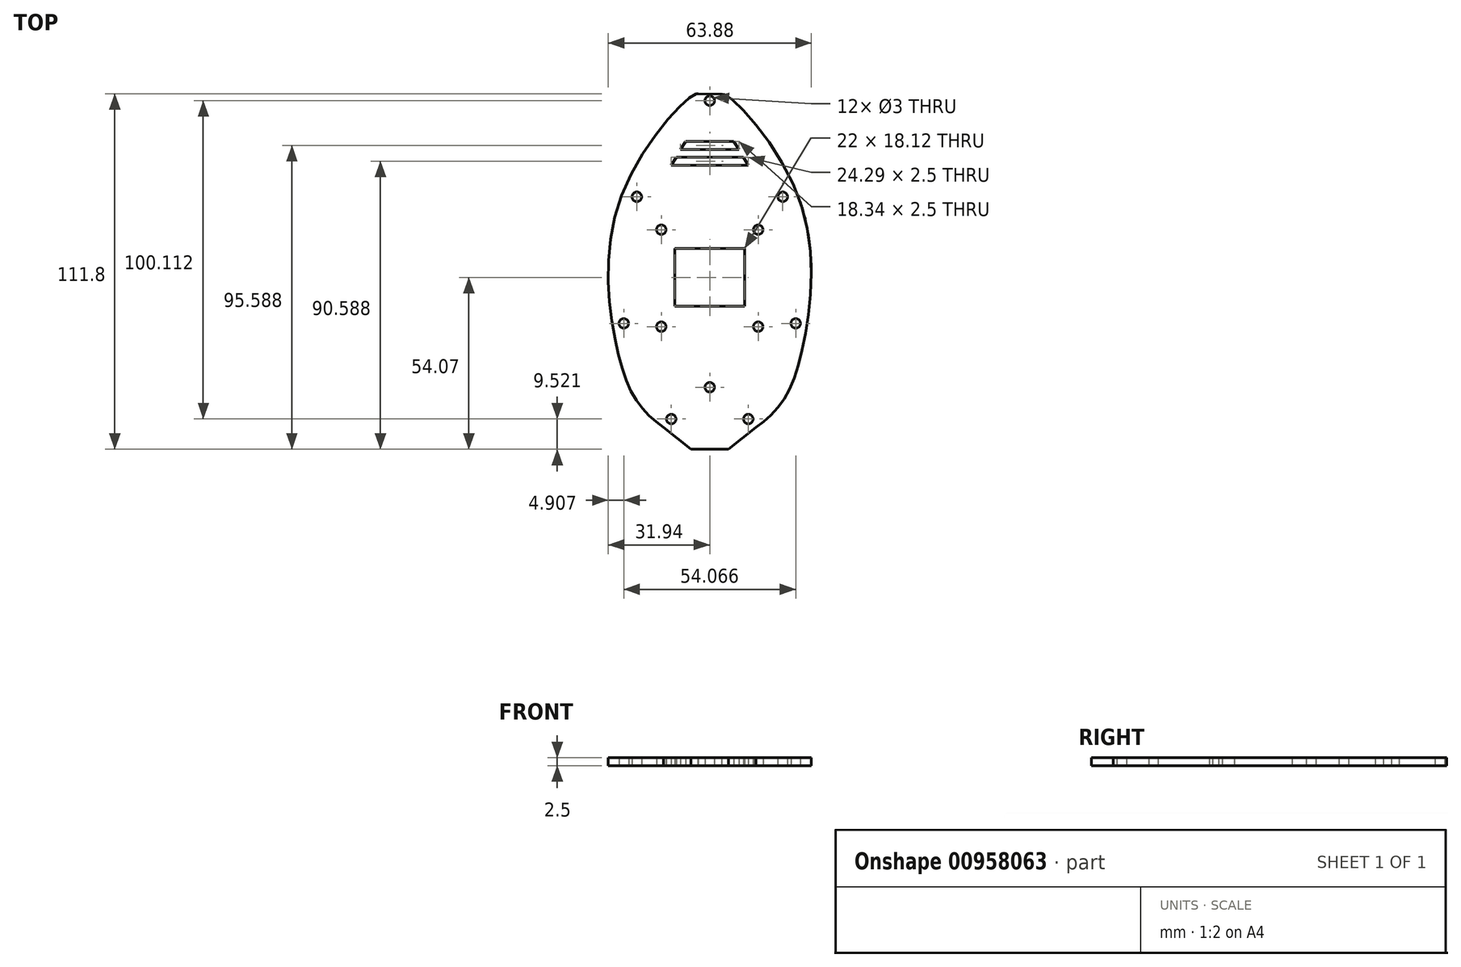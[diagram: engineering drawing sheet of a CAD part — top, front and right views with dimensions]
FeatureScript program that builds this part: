
annotation { "Feature Type Name" : "Feature", "Feature Type Description" : "" }
export const myFeature = defineFeature(function(context is Context, id is Id, definition is map)
    precondition{}
    {
        {
            var Q0;
            Q0=qCreatedBy(makeId("Top.planeOp"),FACE);
            var sketch = newSketch(context, id + "F0", { "sketchPlane" : qUnion([Q0])});
            skCircle(sketch, "E0", {"center": v(-27.03, 3.13) * mm, "radius": 1.5 * mm});
            skCircle(sketch, "E1", {"center": v(-12.12, -26.95) * mm, "radius": 1.5 * mm});
            skCircle(sketch, "E2", {"center": v(-22.94, 42.94) * mm, "radius": 1.5 * mm});
            skCircle(sketch, "E3", {"center": v(0, 73.16) * mm, "radius": 1.5 * mm});
            skCircle(sketch, "E4.MirrorC", {"center": v(22.94, 42.94) * mm, "radius": 1.5 * mm});
            skCircle(sketch, "E5.MirrorC", {"center": v(27.03, 3.13) * mm, "radius": 1.5 * mm});
            skCircle(sketch, "E6.MirrorC", {"center": v(12.12, -26.95) * mm, "radius": 1.5 * mm});
            skFitSpline(sketch, "E7", {"points": [v(-14.57, -29.55) * mm, v(-22.47, -22.07) * mm, v(-29.18, -4.58) * mm, v(-27.39, 44.23) * mm, v(-4.28, 75.27) * mm, v(-3.78, 75.26) * mm], "startDerivative": vector(-53.1, 39.59) * mm, "endDerivative": vector(-15.84, -4.32) * mm});
            skLineSegment(sketch, "E8", {"start": v(-14.57, -29.55) * mm, "end": v(-5.94, -36.47) * mm});
            skLineSegment(sketch, "E9", {"start": v(-5.94, -36.47) * mm, "end": v(0, -36.47) * mm});
            skFitSpline(sketch, "E10.MirrorCS", {"points": [v(14.57, -29.55) * mm, v(22.47, -22.07) * mm, v(29.18, -4.58) * mm, v(27.39, 44.23) * mm, v(4.28, 75.27) * mm, v(3.78, 75.26) * mm], "startDerivative": vector(53.1, 39.59) * mm, "endDerivative": vector(15.84, -4.32) * mm});
            skLineSegment(sketch, "E11.MirrorCS", {"start": v(14.57, -29.55) * mm, "end": v(5.94, -36.47) * mm});
            skLineSegment(sketch, "E12.MirrorCS", {"start": v(5.94, -36.47) * mm, "end": v(0, -36.47) * mm});
            skLineSegment(sketch, "E13", {"start": v(-3.6, 75.31) * mm, "end": v(3.78, 75.26) * mm});
            skCircle(sketch, "E14", {"center": v(-15.25, 32.58) * mm, "radius": 1.5 * mm});
            skCircle(sketch, "E15", {"center": v(-15.25, 2.08) * mm, "radius": 1.5 * mm});
            skCircle(sketch, "E16.MirrorC", {"center": v(15.25, 32.58) * mm, "radius": 1.5 * mm});
            skCircle(sketch, "E17.MirrorC", {"center": v(15.25, 2.08) * mm, "radius": 1.5 * mm});
            skCircle(sketch, "E18", {"center": v(0, -16.97) * mm, "radius": 1.5 * mm});
            skLineSegment(sketch, "E19", {"start": v(-11, 26.66) * mm, "end": v(-11, 8.54) * mm});
            skLineSegment(sketch, "E20", {"start": v(-11, 8.54) * mm, "end": v(11, 8.54) * mm});
            skLineSegment(sketch, "E21", {"start": v(11, 8.54) * mm, "end": v(11, 26.66) * mm});
            skLineSegment(sketch, "E22", {"start": v(11, 26.66) * mm, "end": v(-11, 26.66) * mm});
            skLineSegment(sketch, "E23", {"start": v(-9.17, 57.87) * mm, "end": v(-7.59, 60.37) * mm});
            skLineSegment(sketch, "E24", {"start": v(-12.14, 52.87) * mm, "end": v(-10.56, 55.37) * mm});
            skLineSegment(sketch, "E25.MirrorCS", {"start": v(9.17, 57.87) * mm, "end": v(7.59, 60.37) * mm});
            skLineSegment(sketch, "E26.MirrorCS", {"start": v(12.14, 52.87) * mm, "end": v(10.56, 55.37) * mm});
            skLineSegment(sketch, "E27", {"start": v(-7.59, 60.37) * mm, "end": v(7.59, 60.37) * mm});
            skLineSegment(sketch, "E28", {"start": v(-9.17, 57.87) * mm, "end": v(9.17, 57.87) * mm});
            skLineSegment(sketch, "E29", {"start": v(-10.56, 55.37) * mm, "end": v(10.56, 55.37) * mm});
            skLineSegment(sketch, "E30", {"start": v(-12.14, 52.87) * mm, "end": v(12.14, 52.87) * mm});
            skLineSegment(sketch, "E31", {"start": v(-4.28, 75.27) * mm, "end": v(-3.6, 75.31) * mm});
            skSolve(sketch);
        }
        {
            var Q0;
            Q0=qSketchRegion(id+"F0",true);
            extrude(context, id + "F1", {"entities" : qUnion([Q0]), "depth" : 2.5 * mm, "offsetDistance" : 25 * mm});
        }
    });
